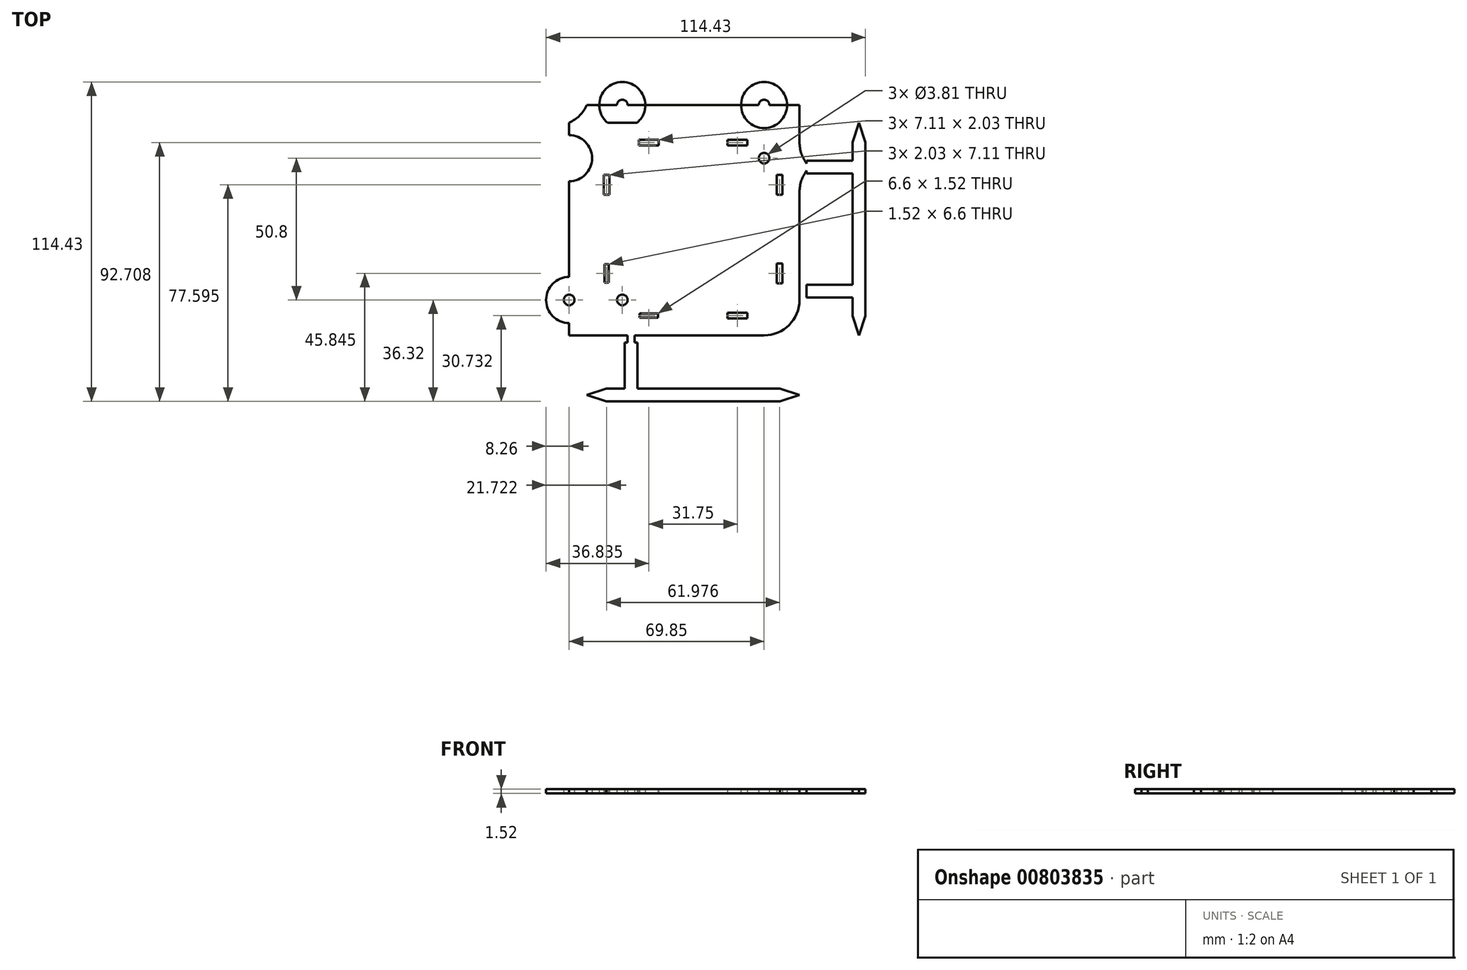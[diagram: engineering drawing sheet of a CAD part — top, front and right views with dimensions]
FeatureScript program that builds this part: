
annotation { "Feature Type Name" : "Feature", "Feature Type Description" : "" }
export const myFeature = defineFeature(function(context is Context, id is Id, definition is map)
    precondition{}
    {
        {
            var Q0;
            Q0=qCreatedBy(makeId("Top.planeOp"),FACE);
            var sketch = newSketch(context, id + "F0", { "sketchPlane" : qUnion([Q0])});
            skLineSegment(sketch, "E0.bottom", {"start": v(38.1, 38.1) * mm, "end": v(-38.1, 38.1) * mm});
            skLineSegment(sketch, "E0.top", {"start": v(38.1, -38.1) * mm, "end": v(-38.1, -38.1) * mm});
            skLineSegment(sketch, "E0.left", {"start": v(38.1, 38.1) * mm, "end": v(38.1, -38.1) * mm});
            skLineSegment(sketch, "E0.right", {"start": v(-38.1, 38.1) * mm, "end": v(-38.1, -38.1) * mm});
            skPoint(sketch, "E0.middle", {"position": v(0, 0) * mm});
            skLineSegment(sketch, "E1.bottom", {"start": v(31.75, 31.75) * mm, "end": v(-31.75, 31.75) * mm, "construction": true});
            skLineSegment(sketch, "E1.top", {"start": v(31.75, -31.75) * mm, "end": v(-31.75, -31.75) * mm, "construction": true});
            skLineSegment(sketch, "E1.left", {"start": v(31.75, 31.75) * mm, "end": v(31.75, -31.75) * mm, "construction": true});
            skLineSegment(sketch, "E1.right", {"start": v(-31.75, 31.75) * mm, "end": v(-31.75, -31.75) * mm, "construction": true});
            skLineSegment(sketch, "E2.bottom", {"start": v(-19.18, -31.75) * mm, "end": v(-12.57, -31.75) * mm});
            skLineSegment(sketch, "E2.top", {"start": v(-19.18, -30.23) * mm, "end": v(-12.57, -30.23) * mm});
            skLineSegment(sketch, "E2.left", {"start": v(-19.18, -31.75) * mm, "end": v(-19.18, -30.23) * mm});
            skLineSegment(sketch, "E2.right", {"start": v(-12.57, -31.75) * mm, "end": v(-12.57, -30.23) * mm});
            skPoint(sketch, "E3", {"position": v(-15.88, -31.75) * mm});
            skLineSegment(sketch, "E4.0", {"start": v(-19.43, -29.97) * mm, "end": v(-12.32, -29.97) * mm});
            skLineSegment(sketch, "E4.1", {"start": v(-19.43, -32) * mm, "end": v(-19.43, -29.97) * mm});
            skLineSegment(sketch, "E4.2", {"start": v(-19.43, -32) * mm, "end": v(-12.32, -32) * mm});
            skLineSegment(sketch, "E4.3", {"start": v(-12.32, -32) * mm, "end": v(-12.32, -29.97) * mm});
            skLineSegment(sketch, "E5.MirrorCS", {"start": v(19.43, -29.97) * mm, "end": v(12.32, -29.97) * mm});
            skLineSegment(sketch, "E6.MirrorCS", {"start": v(19.43, -32) * mm, "end": v(19.43, -29.97) * mm});
            skLineSegment(sketch, "E7.MirrorCS", {"start": v(19.43, -32) * mm, "end": v(12.32, -32) * mm});
            skLineSegment(sketch, "E8.MirrorCS", {"start": v(12.32, -32) * mm, "end": v(12.32, -29.97) * mm});
            skLineSegment(sketch, "E9.MirrorCS", {"start": v(-19.43, 32) * mm, "end": v(-19.43, 29.97) * mm});
            skLineSegment(sketch, "E10.MirrorCS", {"start": v(-19.43, 29.97) * mm, "end": v(-12.32, 29.97) * mm});
            skLineSegment(sketch, "E11.MirrorCS", {"start": v(-12.32, 32) * mm, "end": v(-12.32, 29.97) * mm});
            skLineSegment(sketch, "E12.MirrorCS", {"start": v(-19.43, 32) * mm, "end": v(-12.32, 32) * mm});
            skLineSegment(sketch, "E13.MirrorCS", {"start": v(19.43, 29.97) * mm, "end": v(12.32, 29.97) * mm});
            skLineSegment(sketch, "E14.MirrorCS", {"start": v(19.43, 32) * mm, "end": v(19.43, 29.97) * mm});
            skLineSegment(sketch, "E15.MirrorCS", {"start": v(19.43, 32) * mm, "end": v(12.32, 32) * mm});
            skLineSegment(sketch, "E16.MirrorCS", {"start": v(12.32, 32) * mm, "end": v(12.32, 29.97) * mm});
            skLineSegment(sketch, "E17.bottom", {"start": v(-31.75, -19.18) * mm, "end": v(-30.23, -19.18) * mm});
            skLineSegment(sketch, "E17.top", {"start": v(-31.75, -12.57) * mm, "end": v(-30.23, -12.57) * mm});
            skLineSegment(sketch, "E17.left", {"start": v(-31.75, -19.18) * mm, "end": v(-31.75, -12.57) * mm});
            skLineSegment(sketch, "E17.right", {"start": v(-30.23, -19.18) * mm, "end": v(-30.23, -12.57) * mm});
            skPoint(sketch, "E18", {"position": v(-31.75, -15.88) * mm});
            skLineSegment(sketch, "E19.0", {"start": v(-29.97, -19.43) * mm, "end": v(-29.97, -12.32) * mm});
            skLineSegment(sketch, "E19.1", {"start": v(-32, -19.43) * mm, "end": v(-29.97, -19.43) * mm});
            skLineSegment(sketch, "E19.2", {"start": v(-32, -19.43) * mm, "end": v(-32, -12.32) * mm});
            skLineSegment(sketch, "E19.3", {"start": v(-32, -12.32) * mm, "end": v(-29.97, -12.32) * mm});
            skLineSegment(sketch, "E20.MirrorCS", {"start": v(-32, 19.43) * mm, "end": v(-32, 12.32) * mm});
            skLineSegment(sketch, "E21.MirrorCS", {"start": v(-32, 12.32) * mm, "end": v(-29.97, 12.32) * mm});
            skLineSegment(sketch, "E22.MirrorCS", {"start": v(-29.97, 19.43) * mm, "end": v(-29.97, 12.32) * mm});
            skLineSegment(sketch, "E23.MirrorCS", {"start": v(-32, 19.43) * mm, "end": v(-29.97, 19.43) * mm});
            skLineSegment(sketch, "E24.MirrorCS", {"start": v(32, -19.43) * mm, "end": v(32, -12.32) * mm});
            skLineSegment(sketch, "E25.MirrorCS", {"start": v(32, -12.32) * mm, "end": v(29.97, -12.32) * mm});
            skLineSegment(sketch, "E26.MirrorCS", {"start": v(29.97, -19.43) * mm, "end": v(29.97, -12.32) * mm});
            skLineSegment(sketch, "E27.MirrorCS", {"start": v(32, -19.43) * mm, "end": v(29.97, -19.43) * mm});
            skLineSegment(sketch, "E28.MirrorCS", {"start": v(29.97, 19.43) * mm, "end": v(29.97, 12.32) * mm});
            skLineSegment(sketch, "E29.MirrorCS", {"start": v(32, 12.32) * mm, "end": v(29.97, 12.32) * mm});
            skLineSegment(sketch, "E30.MirrorCS", {"start": v(32, 19.43) * mm, "end": v(32, 12.32) * mm});
            skLineSegment(sketch, "E31.MirrorCS", {"start": v(32, 19.43) * mm, "end": v(29.97, 19.43) * mm});
            skLineSegment(sketch, "E32.bottom", {"start": v(-23.5, -38.1) * mm, "end": v(-20.96, -38.1) * mm});
            skLineSegment(sketch, "E32.top", {"start": v(-23.5, -40.64) * mm, "end": v(-20.96, -40.64) * mm});
            skLineSegment(sketch, "E32.left", {"start": v(-23.5, -38.1) * mm, "end": v(-23.5, -40.64) * mm});
            skLineSegment(sketch, "E32.right", {"start": v(-20.96, -38.1) * mm, "end": v(-20.96, -40.64) * mm});
            skPoint(sketch, "E33", {"position": v(-22.23, -38.1) * mm});
            skLineSegment(sketch, "E34.bottom", {"start": v(-24.51, -40.64) * mm, "end": v(-19.94, -40.64) * mm});
            skLineSegment(sketch, "E34.top", {"start": v(-24.51, -57.15) * mm, "end": v(-19.94, -57.15) * mm});
            skLineSegment(sketch, "E34.left", {"start": v(-24.51, -40.64) * mm, "end": v(-24.51, -57.15) * mm});
            skLineSegment(sketch, "E34.right", {"start": v(-19.94, -40.64) * mm, "end": v(-19.94, -57.15) * mm});
            skPoint(sketch, "E35", {"position": v(-22.23, -40.64) * mm});
            skLineSegment(sketch, "E36.MirrorCS", {"start": v(23.5, -38.1) * mm, "end": v(20.96, -38.1) * mm});
            skPoint(sketch, "E37.MirrorP", {"position": v(22.23, -38.1) * mm});
            skLineSegment(sketch, "E38.bottom", {"start": v(0, -57.15) * mm, "end": v(-31.12, -57.15) * mm});
            skLineSegment(sketch, "E38.top", {"start": v(0, -61.72) * mm, "end": v(-31.12, -61.72) * mm});
            skLineSegment(sketch, "E39", {"start": v(-38.1, -59.44) * mm, "end": v(-31.12, -57.15) * mm});
            skLineSegment(sketch, "E40", {"start": v(-38.1, -59.44) * mm, "end": v(-31.12, -61.72) * mm});
            skPoint(sketch, "E41.start.orphan", {"position": v(-31.12, -59.44) * mm});
            skLineSegment(sketch, "E42.MirrorCS", {"start": v(-38.1, -38.1) * mm, "end": v(-38.1, 38.1) * mm});
            skCircle(sketch, "E43", {"center": v(-25.4, 25.4) * mm, "radius": 1.9 * mm});
            skCircle(sketch, "E44.MirrorC", {"center": v(25.4, 25.4) * mm, "radius": 1.9 * mm});
            skCircle(sketch, "E45.MirrorC", {"center": v(-25.4, -25.4) * mm, "radius": 1.9 * mm});
            skCircle(sketch, "E46.MirrorC", {"center": v(25.4, -25.4) * mm, "radius": 1.9 * mm});
            skLineSegment(sketch, "E47", {"start": v(0, 38.1) * mm, "end": v(0, -38.1) * mm, "construction": true});
            skLineSegment(sketch, "E48", {"start": v(0, -38.1) * mm, "end": v(0, -79.98) * mm, "construction": true});
            skLineSegment(sketch, "E49.MirrorCS", {"start": v(24.51, -40.64) * mm, "end": v(19.94, -40.64) * mm});
            skLineSegment(sketch, "E50.MirrorCS", {"start": v(23.5, -40.64) * mm, "end": v(20.96, -40.64) * mm});
            skLineSegment(sketch, "E51.MirrorCS", {"start": v(23.5, -38.1) * mm, "end": v(23.5, -40.64) * mm});
            skLineSegment(sketch, "E52.MirrorCS", {"start": v(20.96, -38.1) * mm, "end": v(20.96, -40.64) * mm});
            skLineSegment(sketch, "E53.MirrorCS", {"start": v(24.51, -57.15) * mm, "end": v(19.94, -57.15) * mm});
            skPoint(sketch, "E54.MirrorP", {"position": v(22.23, -40.64) * mm});
            skLineSegment(sketch, "E55.MirrorCS", {"start": v(0, -57.15) * mm, "end": v(31.12, -57.15) * mm});
            skLineSegment(sketch, "E56.MirrorCS", {"start": v(38.1, -59.44) * mm, "end": v(31.12, -57.15) * mm});
            skLineSegment(sketch, "E57.MirrorCS", {"start": v(38.1, -59.44) * mm, "end": v(31.12, -61.72) * mm});
            skLineSegment(sketch, "E58.MirrorCS", {"start": v(24.51, -40.64) * mm, "end": v(24.51, -57.15) * mm});
            skLineSegment(sketch, "E59.MirrorCS", {"start": v(0, -61.72) * mm, "end": v(31.12, -61.72) * mm});
            skPoint(sketch, "E60.MirrorP", {"position": v(31.12, -59.44) * mm});
            skLineSegment(sketch, "E61.MirrorCS", {"start": v(19.94, -40.64) * mm, "end": v(19.94, -57.15) * mm});
            skCircle(sketch, "E62", {"center": v(-44.45, -25.4) * mm, "radius": 1.9 * mm});
            skCircle(sketch, "E63.0", {"center": v(-44.45, -25.4) * mm, "radius": 8.25 * mm});
            skLineSegment(sketch, "E64", {"start": v(-38.1, -38.1) * mm, "end": v(-48.31, -32.7) * mm, "construction": true});
            skCircle(sketch, "E65.MirrorC", {"center": v(-44.45, 25.4) * mm, "radius": 8.25 * mm});
            skLineSegment(sketch, "E66.MirrorCS", {"start": v(-38.1, 38.1) * mm, "end": v(-48.31, 32.7) * mm, "construction": true});
            skCircle(sketch, "E67.MirrorC", {"center": v(-44.45, 25.4) * mm, "radius": 1.9 * mm});
            skLineSegment(sketch, "E68", {"start": v(-44.45, 17.14) * mm, "end": v(-44.45, -17.14) * mm});
            skPoint(sketch, "E69.MirrorP", {"position": v(31.75, -15.88) * mm});
            skLineSegment(sketch, "E70.bottom", {"start": v(-38.1, 38.1) * mm, "end": v(-44.45, 38.1) * mm});
            skLineSegment(sketch, "E70.top", {"start": v(-38.1, -38.1) * mm, "end": v(-44.45, -38.1) * mm});
            skLineSegment(sketch, "E70.right", {"start": v(-44.45, 38.1) * mm, "end": v(-44.45, -38.1) * mm});
            skLineSegment(sketch, "E71.1.0", {"start": v(38.1, 0) * mm, "end": v(79.98, 0) * mm, "construction": true});
            skLineSegment(sketch, "E71.1.2", {"start": v(61.72, 0) * mm, "end": v(61.72, -31.12) * mm});
            skLineSegment(sketch, "E71.1.3", {"start": v(61.72, 0) * mm, "end": v(61.72, 31.12) * mm});
            skLineSegment(sketch, "E71.1.4", {"start": v(59.44, -38.1) * mm, "end": v(61.72, -31.12) * mm});
            skLineSegment(sketch, "E71.1.5", {"start": v(59.44, 38.1) * mm, "end": v(57.15, 31.12) * mm});
            skPoint(sketch, "E71.1.6", {"position": v(59.44, -31.12) * mm});
            skLineSegment(sketch, "E71.1.7", {"start": v(59.44, 38.1) * mm, "end": v(61.72, 31.12) * mm});
            skLineSegment(sketch, "E71.1.8", {"start": v(40.64, 24.51) * mm, "end": v(57.15, 24.51) * mm});
            skPoint(sketch, "E71.1.9", {"position": v(38.1, -22.22) * mm});
            skPoint(sketch, "E71.1.10", {"position": v(38.1, 22.23) * mm});
            skLineSegment(sketch, "E71.1.11", {"start": v(57.15, 0) * mm, "end": v(57.15, 31.12) * mm});
            skLineSegment(sketch, "E71.1.12", {"start": v(59.44, -38.1) * mm, "end": v(57.15, -31.12) * mm});
            skLineSegment(sketch, "E71.1.13", {"start": v(40.64, 19.94) * mm, "end": v(57.15, 19.94) * mm});
            skLineSegment(sketch, "E71.1.14", {"start": v(57.15, 0) * mm, "end": v(57.15, -31.12) * mm});
            skPoint(sketch, "E71.1.15", {"position": v(59.44, 31.12) * mm});
            skLineSegment(sketch, "E71.1.16", {"start": v(40.64, -19.94) * mm, "end": v(57.15, -19.94) * mm});
            skPoint(sketch, "E71.1.17", {"position": v(40.64, 22.23) * mm});
            skLineSegment(sketch, "E71.1.18", {"start": v(40.64, -24.51) * mm, "end": v(57.15, -24.51) * mm});
            skPoint(sketch, "E71.1.19", {"position": v(40.64, 22.23) * mm});
            skPoint(sketch, "E71.1.20", {"position": v(38.1, 22.23) * mm});
            skPoint(sketch, "E71.1.21", {"position": v(40.64, -22.22) * mm});
            skLineSegment(sketch, "E71.1.22", {"start": v(57.15, -24.51) * mm, "end": v(57.15, -19.94) * mm});
            skLineSegment(sketch, "E71.1.23", {"start": v(-38.1, 0) * mm, "end": v(38.1, 0) * mm, "construction": true});
            skLineSegment(sketch, "E71.1.24", {"start": v(57.15, 24.51) * mm, "end": v(57.15, 19.94) * mm});
            skLineSegment(sketch, "E71.1.25", {"start": v(-38.1, 38.1) * mm, "end": v(38.1, 38.1) * mm});
            skPoint(sketch, "E71.1.26", {"position": v(40.64, -22.22) * mm});
            skLineSegment(sketch, "E71.1.27", {"start": v(40.64, 24.51) * mm, "end": v(40.64, 19.94) * mm});
            skLineSegment(sketch, "E71.1.28", {"start": v(38.1, -23.5) * mm, "end": v(38.1, -20.95) * mm});
            skLineSegment(sketch, "E71.1.29", {"start": v(38.1, 23.5) * mm, "end": v(40.64, 23.5) * mm});
            skLineSegment(sketch, "E71.1.30", {"start": v(40.64, 23.5) * mm, "end": v(40.64, 20.96) * mm});
            skLineSegment(sketch, "E71.1.31", {"start": v(38.1, -20.95) * mm, "end": v(40.64, -20.95) * mm});
            skLineSegment(sketch, "E71.1.32", {"start": v(40.64, -24.51) * mm, "end": v(40.64, -19.94) * mm});
            skLineSegment(sketch, "E71.1.33", {"start": v(40.64, -23.5) * mm, "end": v(40.64, -20.95) * mm});
            skLineSegment(sketch, "E71.1.34", {"start": v(38.1, -23.5) * mm, "end": v(40.64, -23.5) * mm});
            skLineSegment(sketch, "E71.1.35", {"start": v(38.1, 23.5) * mm, "end": v(38.1, 20.96) * mm});
            skLineSegment(sketch, "E71.1.36", {"start": v(38.1, 20.96) * mm, "end": v(40.64, 20.96) * mm});
            skLineSegment(sketch, "E71.1.37", {"start": v(-38.1, -38.1) * mm, "end": v(38.1, -38.1) * mm});
            skLineSegment(sketch, "E71.1.38", {"start": v(38.1, -38.1) * mm, "end": v(38.1, -44.45) * mm});
            skLineSegment(sketch, "E71.1.39", {"start": v(38.1, 23.5) * mm, "end": v(38.1, 20.96) * mm});
            skLineSegment(sketch, "E71.1.40", {"start": v(38.1, -38.1) * mm, "end": v(32.7, -48.31) * mm});
            skLineSegment(sketch, "E71.1.42", {"start": v(-38.1, -38.1) * mm, "end": v(38.1, -38.1) * mm});
            skLineSegment(sketch, "E71.anchor1", {"start": v(0, 0) * mm, "end": v(-38.1, -59.44) * mm, "construction": true});
            skLineSegment(sketch, "E71.anchor2", {"start": v(0, 0) * mm, "end": v(59.44, -38.1) * mm, "construction": true});
            skPoint(sketch, "E72.center", {"position": v(7.62, 0) * mm});
            skLineSegment(sketch, "E72.anchor1", {"start": v(7.62, 0) * mm, "end": v(-44.45, -38.1) * mm, "construction": true});
            skLineSegment(sketch, "E72.anchor2", {"start": v(7.62, 0) * mm, "end": v(-30.48, 52.07) * mm, "construction": true});
            skLineSegment(sketch, "E73.1.0", {"start": v(38.1, 44.45) * mm, "end": v(-38.1, 44.45) * mm});
            skLineSegment(sketch, "E73.1.3", {"start": v(17.14, 44.45) * mm, "end": v(-17.14, 44.45) * mm});
            skLineSegment(sketch, "E73.1.4", {"start": v(-38.1, 38.1) * mm, "end": v(-32.7, 48.31) * mm, "construction": true});
            skLineSegment(sketch, "E73.1.5", {"start": v(38.1, 38.1) * mm, "end": v(32.7, 48.31) * mm, "construction": true});
            skLineSegment(sketch, "E73.1.6", {"start": v(38.1, 38.1) * mm, "end": v(38.1, 44.45) * mm});
            skCircle(sketch, "E73.1.7", {"center": v(25.4, 44.45) * mm, "radius": 1.9 * mm});
            skCircle(sketch, "E73.1.8", {"center": v(-25.4, 44.45) * mm, "radius": 1.9 * mm});
            skLineSegment(sketch, "E73.1.10", {"start": v(-38.1, 38.1) * mm, "end": v(-38.1, 44.45) * mm});
            skCircle(sketch, "E73.1.11", {"center": v(25.4, 44.45) * mm, "radius": 8.25 * mm});
            skCircle(sketch, "E73.1.12", {"center": v(-25.4, 44.45) * mm, "radius": 8.25 * mm});
            skLineSegment(sketch, "E73.anchor1", {"start": v(0, 0) * mm, "end": v(-44.45, -38.1) * mm, "construction": true});
            skLineSegment(sketch, "E73.anchor2", {"start": v(0, 0) * mm, "end": v(-38.1, 44.45) * mm, "construction": true});
            skSolve(sketch);
        }
        {
            var Q0;
            Q0=makeQuery(id+"F0.imprint","IMPRINT",FACE,{"disambiguationData":[TD([[makeQuery(id+"F0.imprint","IMPRINT",EDGE,{"derivedFrom":sQuery(id+"F0.wireOp",EDGE,"E4.0")}),1.0]])]});
            var Q1;
            Q1=makeQuery(id+"F0.imprint","IMPRINT",FACE,{"disambiguationData":[TD([[makeQuery(id+"F0.imprint","IMPRINT",EDGE,{"derivedFrom":sQuery(id+"F0.wireOp",EDGE,"E38.top")}),-1.0]])]});
            var Q2;
            {var subQ0=sQuery(id+"F0.wireOp",EDGE,"E34.left");Q2=makeQuery(id+"F0.imprint","IMPRINT",FACE,{"disambiguationData":[TD([[makeQuery(id+"F0.imprint","IMPRINT",EDGE,{"derivedFrom":subQ0}),1.0]])]});}
            var Q3;
            {var subQ0=sQuery(id+"F0.wireOp",EDGE,"E50.MirrorCS");Q3=makeQuery(id+"F0.imprint","IMPRINT",FACE,{"disambiguationData":[TD([[makeQuery(id+"F0.imprint","IMPRINT",EDGE,{"derivedFrom":subQ0}),1.0]])]});}
            var Q4;
            Q4=makeQuery(id+"F0.imprint","IMPRINT",FACE,{"disambiguationData":[TD([[makeQuery(id+"F0.imprint","IMPRINT",EDGE,{"derivedFrom":sQuery(id+"F0.wireOp",EDGE,"E50.MirrorCS")}),-1.0]])]});
            var Q5;
            {var subQ0=sQuery(id+"F0.wireOp",EDGE,"E70.right");var subQ1=sQuery(id+"F0.wireOp",EDGE,"E65.MirrorC");var subQ2=makeQuery(id+"F0.imprint","INTERSECT",VERTEX,{"disambiguationData":[OD(0.0)],"derivedFrom":[subQ1,subQ0]});Q5=makeQuery(id+"F0.imprint","IMPRINT",FACE,{"disambiguationData":[TD([[makeQuery(id+"F0.imprint","IMPRINT",EDGE,{"disambiguationData":[TD([[subQ2,-1.0]])],"derivedFrom":subQ1}),-1.0]])]});}
            var Q6;
            {var subQ0=sQuery(id+"F0.wireOp",EDGE,"E70.right");var subQ1=sQuery(id+"F0.wireOp",EDGE,"E62");var subQ2=makeQuery(id+"F0.imprint","INTERSECT",VERTEX,{"disambiguationData":[OD(0.0)],"derivedFrom":[subQ1,subQ0]});Q6=makeQuery(id+"F0.imprint","IMPRINT",FACE,{"disambiguationData":[TD([[makeQuery(id+"F0.imprint","IMPRINT",EDGE,{"disambiguationData":[TD([[subQ2,-1.0]])],"derivedFrom":subQ1}),-1.0]])]});}
            var Q7;
            {var subQ1=sQuery(id+"F0.wireOp",EDGE,"E65.MirrorC");var subQ4=sQuery(id+"F0.wireOp",EDGE,"E70.right");var subQ9=makeQuery(id+"F0.imprint","INTERSECT",VERTEX,{"disambiguationData":[OD(0.0)],"derivedFrom":[subQ1,subQ4]});Q7=makeQuery(id+"F0.imprint","IMPRINT",FACE,{"disambiguationData":[TD([[makeQuery(id+"F0.imprint","IMPRINT",EDGE,{"disambiguationData":[TD([[subQ9,1.0]])],"derivedFrom":subQ1}),-1.0]])]});}
            var Q8;
            {var subQ5=sQuery(id+"F0.wireOp",EDGE,"E70.bottom");Q8=makeQuery(id+"F0.imprint","IMPRINT",FACE,{"disambiguationData":[TD([[makeQuery(id+"F0.imprint","IMPRINT",EDGE,{"derivedFrom":subQ5}),1.0]])]});}
            var Q9;
            {var subQ5=sQuery(id+"F0.wireOp",EDGE,"E70.top");Q9=makeQuery(id+"F0.imprint","IMPRINT",FACE,{"disambiguationData":[TD([[makeQuery(id+"F0.imprint","IMPRINT",EDGE,{"derivedFrom":subQ5}),-1.0]])]});}
            var Q10;
            {var subQ0=sQuery(id+"F0.wireOp",EDGE,"E70.right");var subQ1=sQuery(id+"F0.wireOp",EDGE,"E63.0");var subQ2=makeQuery(id+"F0.imprint","INTERSECT",VERTEX,{"disambiguationData":[OD(0.0)],"derivedFrom":[subQ1,subQ0]});Q10=makeQuery(id+"F0.imprint","IMPRINT",FACE,{"disambiguationData":[TD([[makeQuery(id+"F0.imprint","IMPRINT",EDGE,{"disambiguationData":[TD([[subQ2,1.0]])],"derivedFrom":subQ1}),-1.0]])]});}
            var Q11;
            Q11=makeQuery(id+"F0.imprint","IMPRINT",FACE,{"disambiguationData":[TD([[makeQuery(id+"F0.imprint","IMPRINT",EDGE,{"derivedFrom":sQuery(id+"F0.wireOp",EDGE,"E71.1.29")}),-1.0]])]});
            var Q12;
            {var subQ1=sQuery(id+"F0.wireOp",EDGE,"E71.1.8");Q12=makeQuery(id+"F0.imprint","IMPRINT",FACE,{"disambiguationData":[TD([[makeQuery(id+"F0.imprint","IMPRINT",EDGE,{"derivedFrom":subQ1}),-1.0]])]});}
            var Q13;
            Q13=makeQuery(id+"F0.imprint","IMPRINT",FACE,{"disambiguationData":[TD([[makeQuery(id+"F0.imprint","IMPRINT",EDGE,{"derivedFrom":sQuery(id+"F0.wireOp",EDGE,"E71.1.2")}),-1.0]])]});
            var Q14;
            {var subQ3=sQuery(id+"F0.wireOp",EDGE,"E71.1.16");Q14=makeQuery(id+"F0.imprint","IMPRINT",FACE,{"disambiguationData":[TD([[makeQuery(id+"F0.imprint","IMPRINT",EDGE,{"derivedFrom":subQ3}),-1.0]])]});}
            var Q15;
            Q15=makeQuery(id+"F0.imprint","IMPRINT",FACE,{"disambiguationData":[TD([[makeQuery(id+"F0.imprint","IMPRINT",EDGE,{"derivedFrom":sQuery(id+"F0.wireOp",EDGE,"E71.1.28")}),-1.0]])]});
            var Q16;
            {var subQ0=sQuery(id+"F0.wireOp",EDGE,"E32.left");Q16=makeQuery(id+"F0.imprint","IMPRINT",FACE,{"disambiguationData":[TD([[makeQuery(id+"F0.imprint","IMPRINT",EDGE,{"derivedFrom":subQ0}),1.0]])]});}
            var Q17;
            {var subQ0=sQuery(id+"F0.wireOp",EDGE,"E73.1.12");var subQ4=sQuery(id+"F0.wireOp",EDGE,"E73.1.0");var subQ5=makeQuery(id+"F0.imprint","INTERSECT",VERTEX,{"derivedFrom":[subQ4,subQ0]});Q17=makeQuery(id+"F0.imprint","IMPRINT",FACE,{"disambiguationData":[TD([[makeQuery(id+"F0.imprint","IMPRINT",EDGE,{"disambiguationData":[TD([[subQ5,1.0]])],"derivedFrom":subQ4}),1.0]])]});}
            var Q18;
            {var subQ0=sQuery(id+"F0.wireOp",EDGE,"E0.right");var subQ1=sQuery(id+"F0.wireOp",EDGE,"E63.0");var subQ2=makeQuery(id+"F0.imprint","INTERSECT",VERTEX,{"disambiguationData":[OD(0.0)],"derivedFrom":[subQ1,subQ0]});Q18=makeQuery(id+"F0.imprint","IMPRINT",FACE,{"disambiguationData":[TD([[makeQuery(id+"F0.imprint","IMPRINT",EDGE,{"disambiguationData":[TD([[subQ2,1.0]])],"derivedFrom":subQ1}),1.0]])]});}
            var Q19;
            {var subQ0=sQuery(id+"F0.wireOp",EDGE,"E73.1.12");var subQ1=sQuery(id+"F0.wireOp",EDGE,"E0.bottom");var subQ2=makeQuery(id+"F0.imprint","INTERSECT",VERTEX,{"disambiguationData":[OD(0.0)],"derivedFrom":[subQ1,subQ0]});Q19=makeQuery(id+"F0.imprint","IMPRINT",FACE,{"disambiguationData":[TD([[makeQuery(id+"F0.imprint","IMPRINT",EDGE,{"disambiguationData":[TD([[subQ2,-1.0]])],"derivedFrom":subQ1}),1.0]])]});}
            var Q20;
            {var subQ0=sQuery(id+"F0.wireOp",EDGE,"E73.1.12");var subQ1=sQuery(id+"F0.wireOp",EDGE,"E73.1.0");var subQ5=makeQuery(id+"F0.imprint","INTERSECT",VERTEX,{"derivedFrom":[subQ1,subQ0]});Q20=makeQuery(id+"F0.imprint","IMPRINT",FACE,{"disambiguationData":[TD([[makeQuery(id+"F0.imprint","IMPRINT",EDGE,{"disambiguationData":[TD([[subQ5,1.0]])],"derivedFrom":subQ1}),-1.0]])]});}
            var Q21;
            {var subQ0=sQuery(id+"F0.wireOp",EDGE,"E73.1.10");Q21=makeQuery(id+"F0.imprint","IMPRINT",FACE,{"disambiguationData":[TD([[makeQuery(id+"F0.imprint","IMPRINT",EDGE,{"derivedFrom":subQ0}),-1.0]])]});}
            var Q22;
            {var subQ0=sQuery(id+"F0.wireOp",EDGE,"E73.1.6");Q22=makeQuery(id+"F0.imprint","IMPRINT",FACE,{"disambiguationData":[TD([[makeQuery(id+"F0.imprint","IMPRINT",EDGE,{"derivedFrom":subQ0}),1.0]])]});}
            var Q23;
            {var subQ0=sQuery(id+"F0.wireOp",EDGE,"E70.right");var subQ5=sQuery(id+"F0.wireOp",EDGE,"E62");var subQ9=makeQuery(id+"F0.imprint","INTERSECT",VERTEX,{"disambiguationData":[OD(0.0)],"derivedFrom":[subQ5,subQ0]});Q23=makeQuery(id+"F0.imprint","IMPRINT",FACE,{"disambiguationData":[TD([[makeQuery(id+"F0.imprint","IMPRINT",EDGE,{"disambiguationData":[TD([[subQ9,1.0]])],"derivedFrom":subQ5}),-1.0]])]});}
            var Q24;
            {var subQ0=sQuery(id+"F0.wireOp",EDGE,"E0.right");var subQ1=sQuery(id+"F0.wireOp",EDGE,"E65.MirrorC");var subQ2=makeQuery(id+"F0.imprint","INTERSECT",VERTEX,{"disambiguationData":[OD(0.0)],"derivedFrom":[subQ1,subQ0]});Q24=makeQuery(id+"F0.imprint","IMPRINT",FACE,{"disambiguationData":[TD([[makeQuery(id+"F0.imprint","IMPRINT",EDGE,{"disambiguationData":[TD([[subQ2,1.0]])],"derivedFrom":subQ1}),-1.0]])]});}
            var Q25;
            {var subQ0=sQuery(id+"F0.wireOp",EDGE,"E73.1.3");Q25=makeQuery(id+"F0.imprint","IMPRINT",FACE,{"disambiguationData":[TD([[makeQuery(id+"F0.imprint","IMPRINT",EDGE,{"derivedFrom":subQ0}),1.0]])]});}
            var Q26;
            {var subQ0=sQuery(id+"F0.wireOp",EDGE,"E73.1.11");var subQ1=sQuery(id+"F0.wireOp",EDGE,"E73.1.0");var subQ2=makeQuery(id+"F0.imprint","INTERSECT",VERTEX,{"derivedFrom":[subQ1,subQ0]});Q26=makeQuery(id+"F0.imprint","IMPRINT",FACE,{"disambiguationData":[TD([[makeQuery(id+"F0.imprint","IMPRINT",EDGE,{"disambiguationData":[TD([[subQ2,-1.0]])],"derivedFrom":subQ1}),-1.0]])]});}
            var Q27;
            {var subQ0=sQuery(id+"F0.wireOp",EDGE,"E73.1.11");var subQ4=sQuery(id+"F0.wireOp",EDGE,"E73.1.0");var subQ9=makeQuery(id+"F0.imprint","INTERSECT",VERTEX,{"derivedFrom":[subQ4,subQ0]});Q27=makeQuery(id+"F0.imprint","IMPRINT",FACE,{"disambiguationData":[TD([[makeQuery(id+"F0.imprint","IMPRINT",EDGE,{"disambiguationData":[TD([[subQ9,-1.0]])],"derivedFrom":subQ4}),1.0]])]});}
            var Q28;
            {var subQ0=sQuery(id+"F0.wireOp",EDGE,"E73.1.11");var subQ1=sQuery(id+"F0.wireOp",EDGE,"E0.bottom");var subQ2=makeQuery(id+"F0.imprint","INTERSECT",VERTEX,{"disambiguationData":[OD(0.0)],"derivedFrom":[subQ1,subQ0]});Q28=makeQuery(id+"F0.imprint","IMPRINT",FACE,{"disambiguationData":[TD([[makeQuery(id+"F0.imprint","IMPRINT",EDGE,{"disambiguationData":[TD([[subQ2,-1.0]])],"derivedFrom":subQ1}),1.0]])]});}
            var Q29;
            Q29=makeQuery(id+"F0.imprint","IMPRINT",FACE,{"disambiguationData":[TD([[makeQuery(id+"F0.imprint","IMPRINT",EDGE,{"derivedFrom":sQuery(id+"F0.wireOp",EDGE,"E43")}),1.0]])]});
            var Q30;
            Q30=makeQuery(id+"F0.imprint","IMPRINT",FACE,{"disambiguationData":[TD([[makeQuery(id+"F0.imprint","IMPRINT",EDGE,{"derivedFrom":sQuery(id+"F0.wireOp",EDGE,"E45.MirrorC")}),-1.0]])]});
            var Q31;
            Q31=makeQuery(id+"F0.imprint","IMPRINT",FACE,{"disambiguationData":[TD([[makeQuery(id+"F0.imprint","IMPRINT",EDGE,{"derivedFrom":sQuery(id+"F0.wireOp",EDGE,"E44.MirrorC")}),-1.0]])]});
            var Q32;
            Q32=makeQuery(id+"F0.imprint","IMPRINT",FACE,{"disambiguationData":[TD([[makeQuery(id+"F0.imprint","IMPRINT",EDGE,{"derivedFrom":sQuery(id+"F0.wireOp",EDGE,"E46.MirrorC")}),1.0]])]});
            var Q33;
            Q33=makeQuery(id+"F0.imprint","IMPRINT",FACE,{"disambiguationData":[TD([[makeQuery(id+"F0.imprint","IMPRINT",EDGE,{"derivedFrom":sQuery(id+"F0.wireOp",EDGE,"E2.bottom")}),-1.0]])]});
            var Q34;
            Q34=makeQuery(id+"F0.imprint","IMPRINT",FACE,{"disambiguationData":[TD([[makeQuery(id+"F0.imprint","IMPRINT",EDGE,{"derivedFrom":sQuery(id+"F0.wireOp",EDGE,"E17.bottom")}),-1.0]])]});
            extrude(context, id + "F1", {"entities" : qUnion([Q0, Q1, Q2, Q3, Q4, Q5, Q6, Q7, Q8, Q9, Q10, Q11, Q12, Q13, Q14, Q15, Q16, Q17, Q18, Q19, Q20, Q21, Q22, Q23, Q24, Q25, Q26, Q27, Q28, Q29, Q30, Q31, Q32, Q33, Q34]), "depth" : 1.52 * mm, "offsetDistance" : 25.4 * mm});
        }
        {
            var Q0;
            Q0=makeQuery(id+"F1.opExtrude","SWEPT_EDGE",EDGE,{"disambiguationData":[OSD([sQuery(id+"F0.wireOp",EDGE,"E0.left"),sQuery(id+"F0.wireOp",EDGE,"E71.1.42")])]});
            var Q1;
            Q1=makeQuery(id+"F1.opExtrude","SWEPT_EDGE",EDGE,{"disambiguationData":[OSD([sQuery(id+"F0.wireOp",EDGE,"E66.MirrorCS"),sQuery(id+"F0.wireOp",EDGE,"E70.bottom"),sQuery(id+"F0.wireOp",EDGE,"E0.right"),sQuery(id+"F0.wireOp",EDGE,"E72.1.7"),sQuery(id+"F0.wireOp",EDGE,"E72.1.8"),sQuery(id+"F0.wireOp",EDGE,"E72.1.12")])]});
            fillet(context, id + "F2", {"entities" : qUnion([Q0, Q1]), "radius" : 12.7 * mm, "tangentPropagation" : true, "allowEdgeOverflow" : false});
        }
    });
